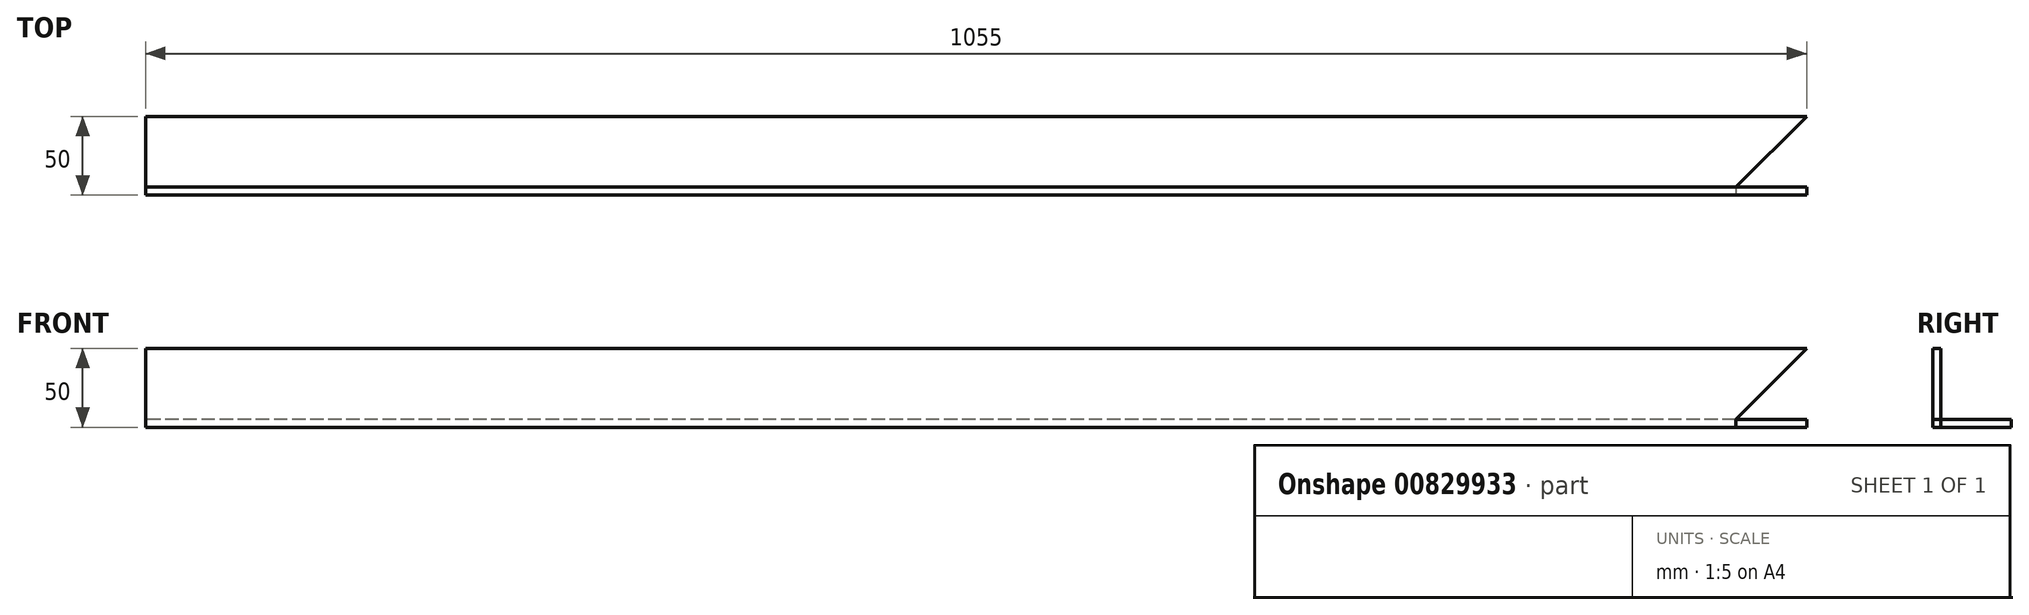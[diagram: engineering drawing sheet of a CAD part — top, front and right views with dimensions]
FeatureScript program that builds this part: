
annotation { "Feature Type Name" : "Feature", "Feature Type Description" : "" }
export const myFeature = defineFeature(function(context is Context, id is Id, definition is map)
    precondition{}
    {
        {
            var Q0;
            Q0=qCreatedBy(makeId("Right.planeOp"),FACE);
            var sketch = newSketch(context, id + "F0", { "sketchPlane" : qUnion([Q0])});
            skLineSegment(sketch, "E0", {"start": v(0, 0) * mm, "end": v(0, 50) * mm});
            skLineSegment(sketch, "E1", {"start": v(0, 50) * mm, "end": v(5, 50) * mm});
            skLineSegment(sketch, "E2", {"start": v(5, 50) * mm, "end": v(5, 5) * mm});
            skLineSegment(sketch, "E3", {"start": v(5, 5) * mm, "end": v(50, 5) * mm});
            skLineSegment(sketch, "E4", {"start": v(50, 5) * mm, "end": v(50, 0) * mm});
            skLineSegment(sketch, "E5", {"start": v(50, 0) * mm, "end": v(0, 0) * mm});
            skSolve(sketch);
        }
        {
            var Q0;
            Q0=makeQuery(id+"F0.imprint","IMPRINT",FACE,{"disambiguationData":[TD([[makeQuery(id+"F0.imprint","IMPRINT",EDGE,{"derivedFrom":sQuery(id+"F0.wireOp",EDGE,"E0")}),-1.0]])]});
            extrude(context, id + "F1", {"entities" : qUnion([Q0]), "depth" : 1055 * mm, "offsetDistance" : 25 * mm});
        }
        {
            var Q0;
            Q0=makeQuery(id+"F1.opExtrude","SWEPT_FACE",FACE,{"disambiguationData":[OSD([sQuery(id+"F0.wireOp",EDGE,"E2")])]});
            var sketch = newSketch(context, id + "F2", { "sketchPlane" : qUnion([Q0])});
            skLineSegment(sketch, "E6", {"start": v(-1010, 5) * mm, "end": v(-1055, 50) * mm});
            skSolve(sketch);
        }
        {
            var Q0;
            Q0=makeQuery(id+"F1.opExtrude","SWEPT_FACE",FACE,{"disambiguationData":[OSD([sQuery(id+"F0.wireOp",EDGE,"E3")])]});
            var sketch = newSketch(context, id + "F3", { "sketchPlane" : qUnion([Q0])});
            skLineSegment(sketch, "E7", {"start": v(1055, 50) * mm, "end": v(1010, 5) * mm});
            skSolve(sketch);
        }
        {
            var Q0;
            {var subQ0=sQuery(id+"F3.wireOp",EDGE,"E7");Q0=makeQuery(id+"F3.imprint","IMPRINT",FACE,{"disambiguationData":[TD([[makeQuery(id+"F3.imprint","IMPRINT",EDGE,{"derivedFrom":subQ0}),1.0]])]});}
            extrude(context, id + "F4", {"entities" : qUnion([Q0]), "operationType" : NewBodyOperationType.REMOVE, "oppositeDirection" : true, "depth" : 5 * mm, "offsetDistance" : 25 * mm});
        }
        {
            var Q0;
            {var subQ0=sQuery(id+"F2.wireOp",EDGE,"E6");Q0=makeQuery(id+"F2.imprint","IMPRINT",FACE,{"disambiguationData":[TD([[makeQuery(id+"F2.imprint","IMPRINT",EDGE,{"derivedFrom":subQ0}),1.0]])]});}
            extrude(context, id + "F5", {"entities" : qUnion([Q0]), "operationType" : NewBodyOperationType.REMOVE, "oppositeDirection" : true, "depth" : 25 * mm, "offsetDistance" : 25 * mm});
        }
        {
            var Q0;
            Q0=makeQuery(id+"F1.opExtrude","CAP_FACE",FACE,{"disambiguationData":[OSD([sQuery(id+"F0.wireOp",EDGE,"E0"),sQuery(id+"F0.wireOp",EDGE,"E1"),sQuery(id+"F0.wireOp",EDGE,"E2"),sQuery(id+"F0.wireOp",EDGE,"E3"),sQuery(id+"F0.wireOp",EDGE,"E4"),sQuery(id+"F0.wireOp",EDGE,"E5")])],"isStart":false});
            extrude(context, id + "F6", {"entities" : qUnion([Q0]), "operationType" : NewBodyOperationType.REMOVE, "oppositeDirection" : true, "depth" : 45 * mm, "offsetDistance" : 25 * mm});
        }
    });
